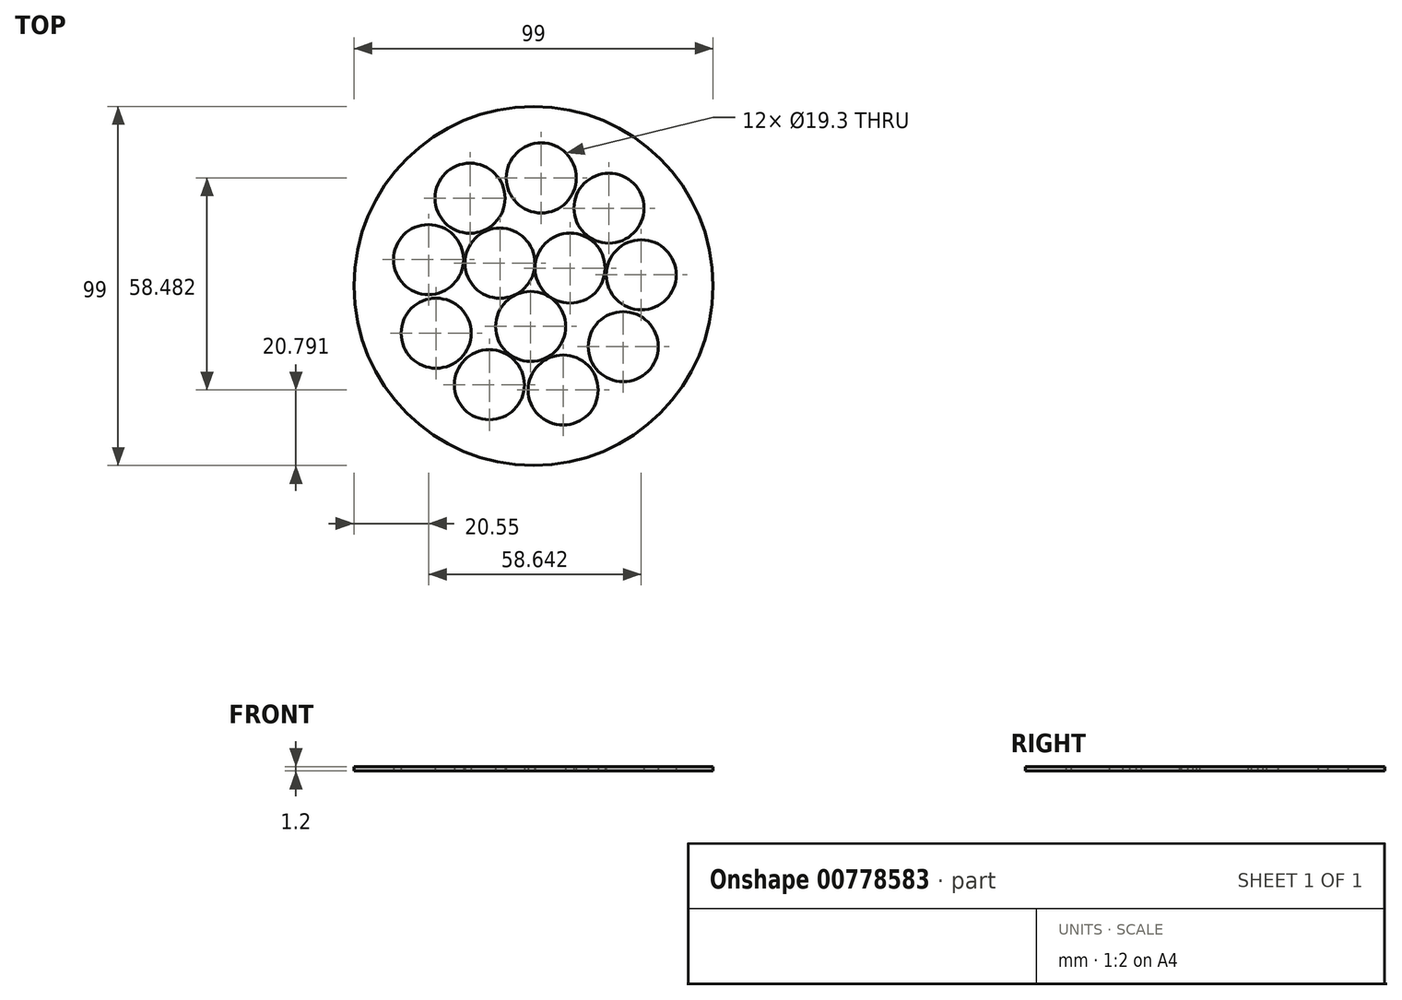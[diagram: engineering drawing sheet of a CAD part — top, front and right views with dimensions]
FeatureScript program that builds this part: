
annotation { "Feature Type Name" : "Feature", "Feature Type Description" : "" }
export const myFeature = defineFeature(function(context is Context, id is Id, definition is map)
    precondition{}
    {
        {
            var Q0;
            Q0=qCreatedBy(makeId("Top.planeOp"),FACE);
            var sketch = newSketch(context, id + "F0", { "sketchPlane" : qUnion([Q0])});
            skCircle(sketch, "E0", {"center": v(0, 0) * mm, "radius": 39.5 * mm});
            skCircle(sketch, "E1", {"center": v(0, 0) * mm, "radius": 49.5 * mm});
            skCircle(sketch, "E2", {"center": v(2.14, 29.77) * mm, "radius": 9.65 * mm});
            skCircle(sketch, "E3", {"center": v(20.78, 21.43) * mm, "radius": 9.65 * mm});
            skCircle(sketch, "E4", {"center": v(29.7, 3.06) * mm, "radius": 9.65 * mm});
            skCircle(sketch, "E5", {"center": v(24.72, -16.74) * mm, "radius": 9.65 * mm});
            skCircle(sketch, "E6", {"center": v(8.17, -28.7) * mm, "radius": 9.65 * mm});
            skCircle(sketch, "E7", {"center": v(-12.2, -27.25) * mm, "radius": 9.65 * mm});
            skCircle(sketch, "E8", {"center": v(-26.85, -13.03) * mm, "radius": 9.65 * mm});
            skCircle(sketch, "E9", {"center": v(-28.95, 7.28) * mm, "radius": 9.65 * mm});
            skCircle(sketch, "E10", {"center": v(-17.5, 24.18) * mm, "radius": 9.65 * mm});
            skPoint(sketch, "E11", {"position": v(-23.22, 15.73) * mm});
            skPoint(sketch, "E12", {"position": v(25.23, 12.25) * mm});
            skPoint(sketch, "E13", {"position": v(-2, -27.98) * mm});
            skCircle(sketch, "E14", {"center": v(-9.27, 6.28) * mm, "radius": 9.65 * mm});
            skCircle(sketch, "E15", {"center": v(10.08, 4.9) * mm, "radius": 9.65 * mm});
            skCircle(sketch, "E16", {"center": v(-0.8, -11.17) * mm, "radius": 9.65 * mm});
            skSolve(sketch);
        }
        {
            var Q0;
            Q0=makeQuery(id+"F0.imprint","IMPRINT",FACE,{"disambiguationData":[TD([[makeQuery(id+"F0.imprint","IMPRINT",EDGE,{"derivedFrom":sQuery(id+"F0.wireOp",EDGE,"E1")}),1.0]])]});
            var Q1;
            {var subQ0=sQuery(id+"F0.wireOp",EDGE,"E2");Q1=makeQuery(id+"F0.imprint","IMPRINT",FACE,{"disambiguationData":[TD([[makeQuery(id+"F0.imprint","IMPRINT",EDGE,{"derivedFrom":subQ0}),-1.0]])]});}
            extrude(context, id + "F1", {"entities" : qUnion([Q0, Q1]), "depth" : 1.2 * mm, "offsetDistance" : 25 * mm});
        }
    });
